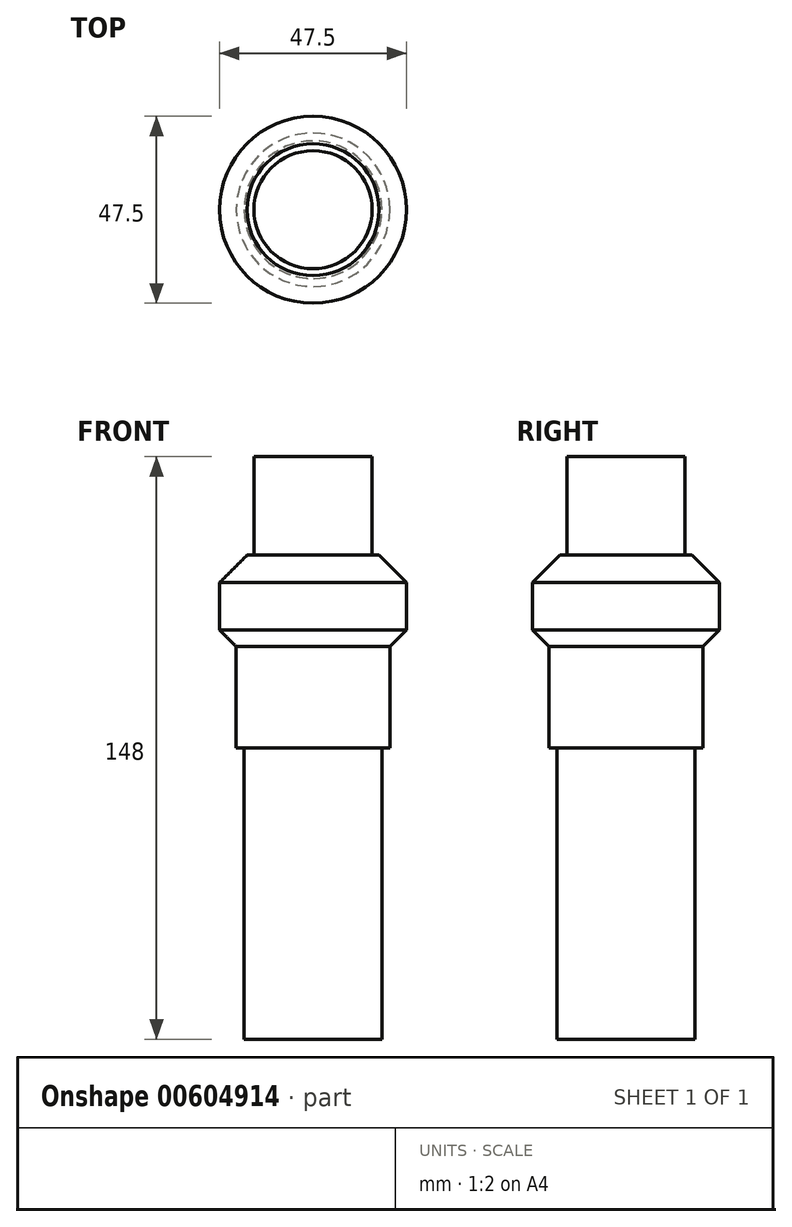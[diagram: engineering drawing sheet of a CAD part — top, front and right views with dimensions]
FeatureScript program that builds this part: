
annotation { "Feature Type Name" : "Feature", "Feature Type Description" : "" }
export const myFeature = defineFeature(function(context is Context, id is Id, definition is map)
    precondition{}
    {
        {
            var Q0;
            Q0=qCreatedBy(makeId("Top.planeOp"),FACE);
            var sketch = newSketch(context, id + "F0", { "sketchPlane" : qUnion([Q0])});
            skCircle(sketch, "E0", {"center": v(0, 0) * mm, "radius": 17.5 * mm});
            skSolve(sketch);
        }
        {
            var Q0;
            Q0 = qSketchRegion(id + "F0", true);
            extrude(context, id + "F1", {"entities" : qUnion([Q0]), "depth" : 75 * mm, "offsetDistance" : 25 * mm});
        }
        {
            var Q0;
            Q0=qCreatedBy(makeId("Front.planeOp"),FACE);
            var sketch = newSketch(context, id + "F2", { "sketchPlane" : qUnion([Q0])});
            skLineSegment(sketch, "E1", {"start": v(0, 0) * mm, "end": v(0, 81.4) * mm, "construction": true});
            skLineSegment(sketch, "E2", {"start": v(0, 74) * mm, "end": v(-19.5, 74) * mm});
            skLineSegment(sketch, "E3", {"start": v(-19.5, 74) * mm, "end": v(-19.5, 99.75) * mm});
            skLineSegment(sketch, "E4", {"start": v(-19.5, 99.75) * mm, "end": v(-23.75, 104) * mm});
            skLineSegment(sketch, "E5", {"start": v(-23.75, 104) * mm, "end": v(-23.75, 116) * mm});
            skLineSegment(sketch, "E6", {"start": v(-23.75, 116) * mm, "end": v(-16.75, 123) * mm});
            skLineSegment(sketch, "E7", {"start": v(-16.75, 123) * mm, "end": v(0, 123) * mm});
            skLineSegment(sketch, "E8", {"start": v(0, 123) * mm, "end": v(0, 74) * mm});
            skSolve(sketch);
        }
        {
            var Q0;
            Q0 = qSketchRegion(id + "F2", true);
            var Q1;
            Q1=sQuery(id+"F2.wireOp",EDGE,"E1");
            revolve(context, id + "F3", {"operationType" : NewBodyOperationType.ADD, "entities" : qUnion([Q0]), "axis" : qUnion([Q1]), "revolveType" : RevolveType.FULL});
        }
        {
            var Q0;
            Q0=makeQuery(id+"F3.opRevolve","SWEPT_FACE",FACE,{"disambiguationData":[OSD([sQuery(id+"F2.wireOp",EDGE,"E7")])]});
            var sketch = newSketch(context, id + "F4", { "sketchPlane" : qUnion([Q0])});
            skCircle(sketch, "E9", {"center": v(0, 0) * mm, "radius": 15 * mm});
            skSolve(sketch);
        }
        {
            var Q0;
            Q0 = qSketchRegion(id + "F4", true);
            extrude(context, id + "F5", {"entities" : qUnion([Q0]), "operationType" : NewBodyOperationType.ADD, "depth" : 25 * mm, "offsetDistance" : 25 * mm});
        }
    });
